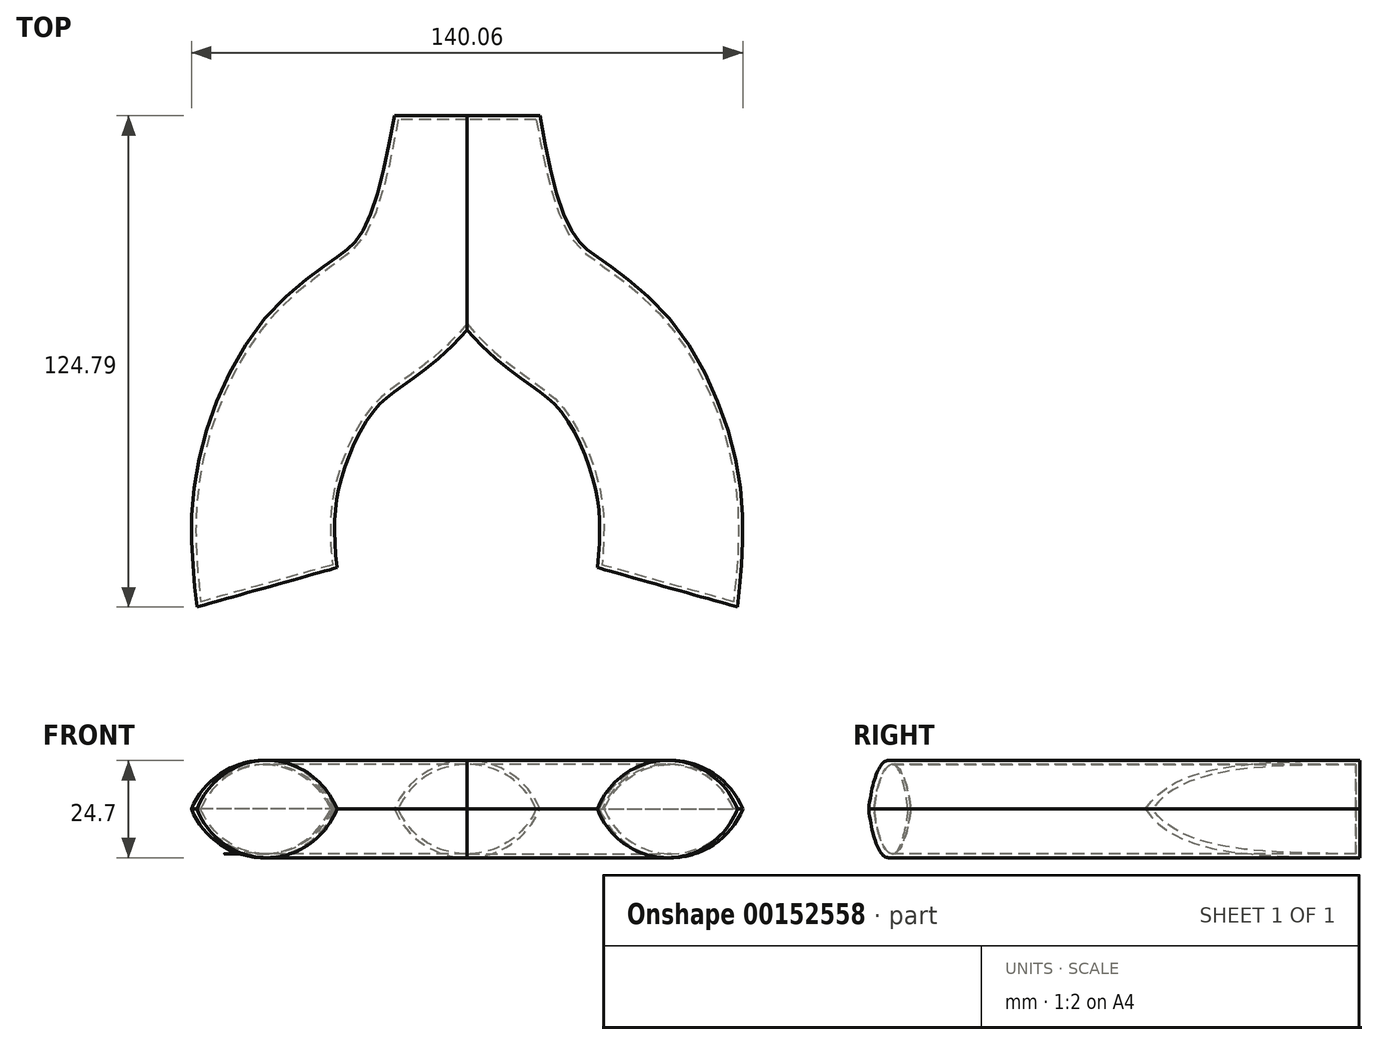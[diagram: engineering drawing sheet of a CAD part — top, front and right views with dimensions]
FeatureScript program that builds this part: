
annotation { "Feature Type Name" : "Feature", "Feature Type Description" : "" }
export const myFeature = defineFeature(function(context is Context, id is Id, definition is map)
    precondition{}
    {
        {
            var Q0;
            Q0=qCreatedBy(makeId("Front.planeOp"),FACE);
            var sketch = newSketch(context, id + "F0", { "sketchPlane" : qUnion([Q0])});
            skArc(sketch, "E0", {"start": v(18.48, 0) * mm, "mid": v(0, 12.35) * mm, "end": v(-18.48, 0) * mm});
            skLineSegment(sketch, "E1", {"start": v(-18.48, 0) * mm, "end": v(18.48, 0) * mm});
            skSolve(sketch);
        }
        {
            var Q0;
            Q0=qCreatedBy(makeId("Top.planeOp"),FACE);
            var sketch = newSketch(context, id + "F1", { "sketchPlane" : qUnion([Q0])});
            skFitSpline(sketch, "E2", {"points": [v(0, 0) * mm, v(-13.13, -41.57) * mm, v(-36.1, -61.81) * mm, v(-50.87, -94.09) * mm, v(-50.87, -119.8) * mm], "startDerivative": vector(-29.83, -166.73) * mm, "endDerivative": vector(10.84, -111.74) * mm});
            skFitSpline(sketch, "E3.MirrorCS", {"points": [v(0, 0) * mm, v(13.13, -41.57) * mm, v(36.1, -61.81) * mm, v(50.87, -94.09) * mm, v(50.87, -119.8) * mm], "startDerivative": vector(29.83, -166.73) * mm, "endDerivative": vector(-10.84, -111.74) * mm});
            skSolve(sketch);
        }
        {
            var Q0;
            Q0=makeQuery(id+"F0.imprint","IMPRINT",FACE,{"disambiguationData":[TD([[makeQuery(id+"F0.imprint","IMPRINT",EDGE,{"derivedFrom":sQuery(id+"F0.wireOp",EDGE,"E0")}),1.0]])]});
            var Q1;
            Q1=sQuery(id+"F1.wireOp",EDGE,"E2");
            sweep(context, id + "F2", {"profiles" : qUnion([Q0]), "path" : qUnion([Q1])});
        }
        {
            var Q0;
            Q0 = qSketchRegion(id + "F0", true);
            var Q1;
            Q1=sQuery(id+"F1.wireOp",EDGE,"E3.MirrorCS");
            sweep(context, id + "F3", {"operationType" : NewBodyOperationType.ADD, "profiles" : qUnion([Q0]), "path" : qUnion([Q1])});
        }
        {
            var Q0;
            {var subQ0=sQuery(id+"F0.wireOp",EDGE,"E1");Q0=makeQuery(id+"F3.boolean.opBoolean","MERGE",FACE,{"derivedFrom":[makeQuery(id+"F2.opSweep","SWEPT_FACE",FACE,{"disambiguationData":[OSD([subQ0,sQuery(id+"F1.wireOp",EDGE,"E2")])]}),makeQuery(id+"F3.opSweep","SWEPT_FACE",FACE,{"disambiguationData":[OSD([subQ0,sQuery(id+"F1.wireOp",EDGE,"E3.MirrorCS")])]})]});}
            shell(context, id + "F4", {"entities" : qUnion([Q0]), "thickness" : 1 * mm});
        }
        {
            var Q0;
            Q0=makeQuery(id+"F2.opSweep","SWEPT_BODY",BODY,{"disambiguationData":[OSD([sQuery(id+"F0.wireOp",EDGE,"E0"),sQuery(id+"F0.wireOp",EDGE,"E1"),sQuery(id+"F1.wireOp",EDGE,"E2")])]});
            var Q1;
            Q1=qCreatedBy(makeId("Top.planeOp"),FACE);
            mirror(context, id + "F5", {"operationType" : NewBodyOperationType.ADD, "entities" : qUnion([Q0]), "mirrorPlane" : qUnion([Q1])});
        }
    });
